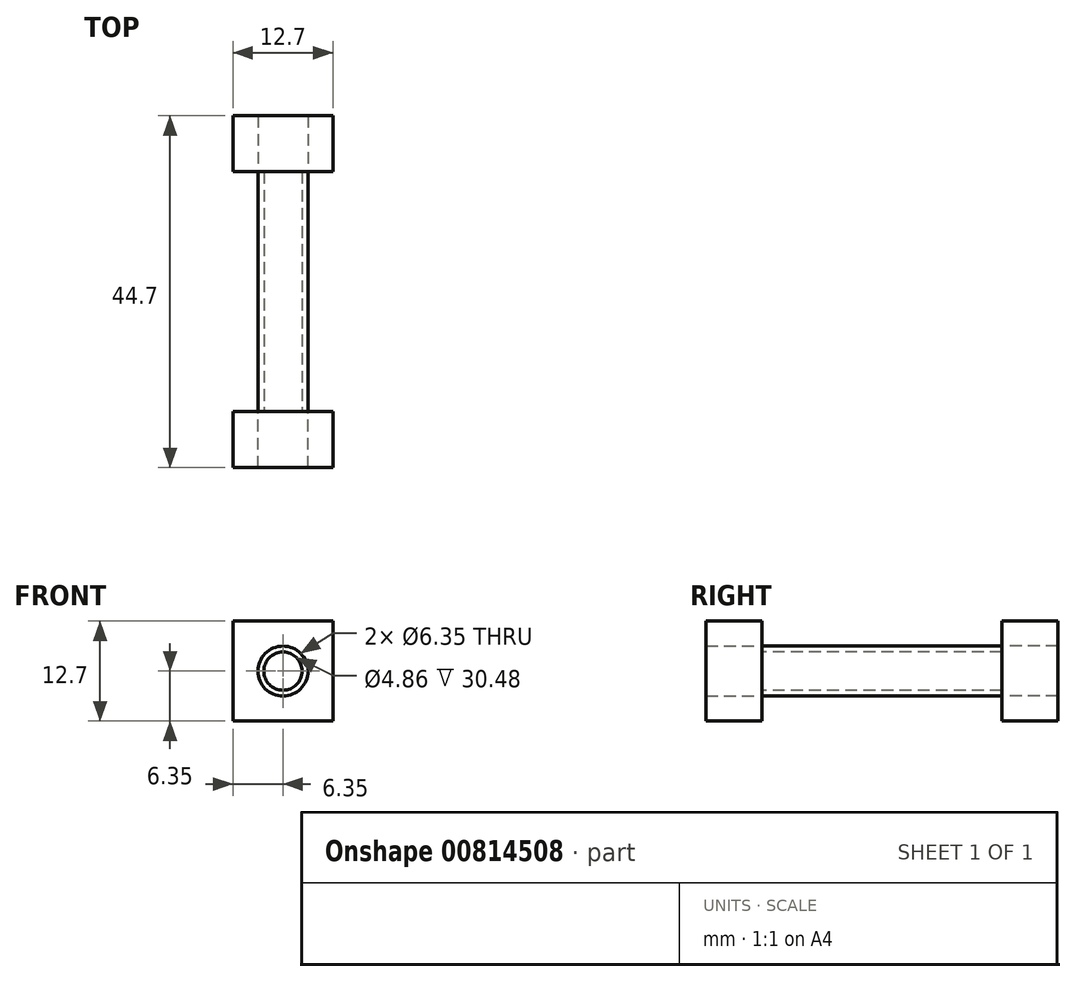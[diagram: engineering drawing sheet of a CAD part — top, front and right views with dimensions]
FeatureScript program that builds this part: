
annotation { "Feature Type Name" : "Feature", "Feature Type Description" : "" }
export const myFeature = defineFeature(function(context is Context, id is Id, definition is map)
    precondition{}
    {
        {
            var Q0;
            Q0=qCreatedBy(makeId("Front.planeOp"),FACE);
            var sketch = newSketch(context, id + "F0", { "sketchPlane" : qUnion([Q0])});
            skCircle(sketch, "E0", {"center": v(0, 0) * mm, "radius": 3.18 * mm});
            skSolve(sketch);
        }
        {
            var Q0;
            Q0=qSketchRegion(id+"F0",true);
            extrude(context, id + "F1", {"entities" : qUnion([Q0]), "depth" : 30.48 * mm, "offsetDistance" : 25.4 * mm});
        }
        {
            var Q0;
            Q0=makeQuery(id+"F1.opExtrude","CAP_FACE",FACE,{"disambiguationData":[OSD([sQuery(id+"F0.wireOp",EDGE,"E0")])],"isStart":true});
            var sketch = newSketch(context, id + "F2", { "sketchPlane" : qUnion([Q0])});
            skSolve(sketch);
        }
        {
            var Q0;
            Q0=makeQuery(id+"F2.imprint","IMPRINT",FACE,{"disambiguationData":[TD([[makeQuery(id+"F2.imprint","IMPRINT",EDGE,{"derivedFrom":makeQuery(id+"F1.opExtrude","CAP_EDGE",EDGE,{"disambiguationData":[OSD([sQuery(id+"F0.wireOp",EDGE,"E0")])],"isStart":true})}),-1.0]])]});
            var sketch = newSketch(context, id + "F3", { "sketchPlane" : qUnion([Q0])});
            skLineSegment(sketch, "E1.bottom", {"start": v(6.35, -6.35) * mm, "end": v(-6.35, -6.35) * mm});
            skLineSegment(sketch, "E1.top", {"start": v(6.35, 6.35) * mm, "end": v(-6.35, 6.35) * mm});
            skLineSegment(sketch, "E1.left", {"start": v(6.35, -6.35) * mm, "end": v(6.35, 6.35) * mm});
            skLineSegment(sketch, "E1.right", {"start": v(-6.35, -6.35) * mm, "end": v(-6.35, 6.35) * mm});
            skSolve(sketch);
        }
        {
            var Q0;
            Q0=makeQuery(id+"F3.imprint","IMPRINT",FACE,{"disambiguationData":[TD([[makeQuery(id+"F3.imprint","IMPRINT",EDGE,{"derivedFrom":sQuery(id+"F3.wireOp",EDGE,"E1.bottom")}),-1.0]])]});
            extrude(context, id + "F4", {"entities" : qUnion([Q0]), "depth" : 7.11 * mm, "offsetDistance" : 25.4 * mm});
        }
        {
            var Q0;
            Q0=makeQuery(id+"F1.opExtrude","CAP_FACE",FACE,{"disambiguationData":[OSD([sQuery(id+"F0.wireOp",EDGE,"E0")])],"isStart":false});
            var sketch = newSketch(context, id + "F5", { "sketchPlane" : qUnion([Q0])});
            skLineSegment(sketch, "E2.bottom", {"start": v(-6.35, 6.35) * mm, "end": v(6.35, 6.35) * mm});
            skLineSegment(sketch, "E2.top", {"start": v(-6.35, -6.35) * mm, "end": v(6.35, -6.35) * mm});
            skLineSegment(sketch, "E2.left", {"start": v(-6.35, 6.35) * mm, "end": v(-6.35, -6.35) * mm});
            skLineSegment(sketch, "E2.right", {"start": v(6.35, 6.35) * mm, "end": v(6.35, -6.35) * mm});
            skSolve(sketch);
        }
        {
            var Q0;
            Q0=makeQuery(id+"F5.imprint","IMPRINT",FACE,{"disambiguationData":[TD([[makeQuery(id+"F5.imprint","IMPRINT",EDGE,{"derivedFrom":sQuery(id+"F5.wireOp",EDGE,"E2.bottom")}),-1.0]])]});
            extrude(context, id + "F6", {"entities" : qUnion([Q0]), "depth" : 7.11 * mm, "offsetDistance" : 25.4 * mm});
        }
        {
            var Q0;
            Q0=makeQuery(id+"F1.opExtrude","CAP_FACE",FACE,{"disambiguationData":[OSD([sQuery(id+"F0.wireOp",EDGE,"E0")])],"isStart":false});
            var sketch = newSketch(context, id + "F7", { "sketchPlane" : qUnion([Q0])});
            skCircle(sketch, "E3", {"center": v(0, 0) * mm, "radius": 2.43 * mm});
            skSolve(sketch);
        }
        {
            var Q0;
            Q0=makeQuery(id+"F7.imprint","IMPRINT",FACE,{"disambiguationData":[TD([[makeQuery(id+"F7.imprint","IMPRINT",EDGE,{"derivedFrom":sQuery(id+"F7.wireOp",EDGE,"E3")}),1.0]])]});
            extrude(context, id + "F8", {"entities" : qUnion([Q0]), "operationType" : NewBodyOperationType.REMOVE, "oppositeDirection" : true, "depth" : 43.69 * mm, "offsetDistance" : 25.4 * mm});
        }
    });
